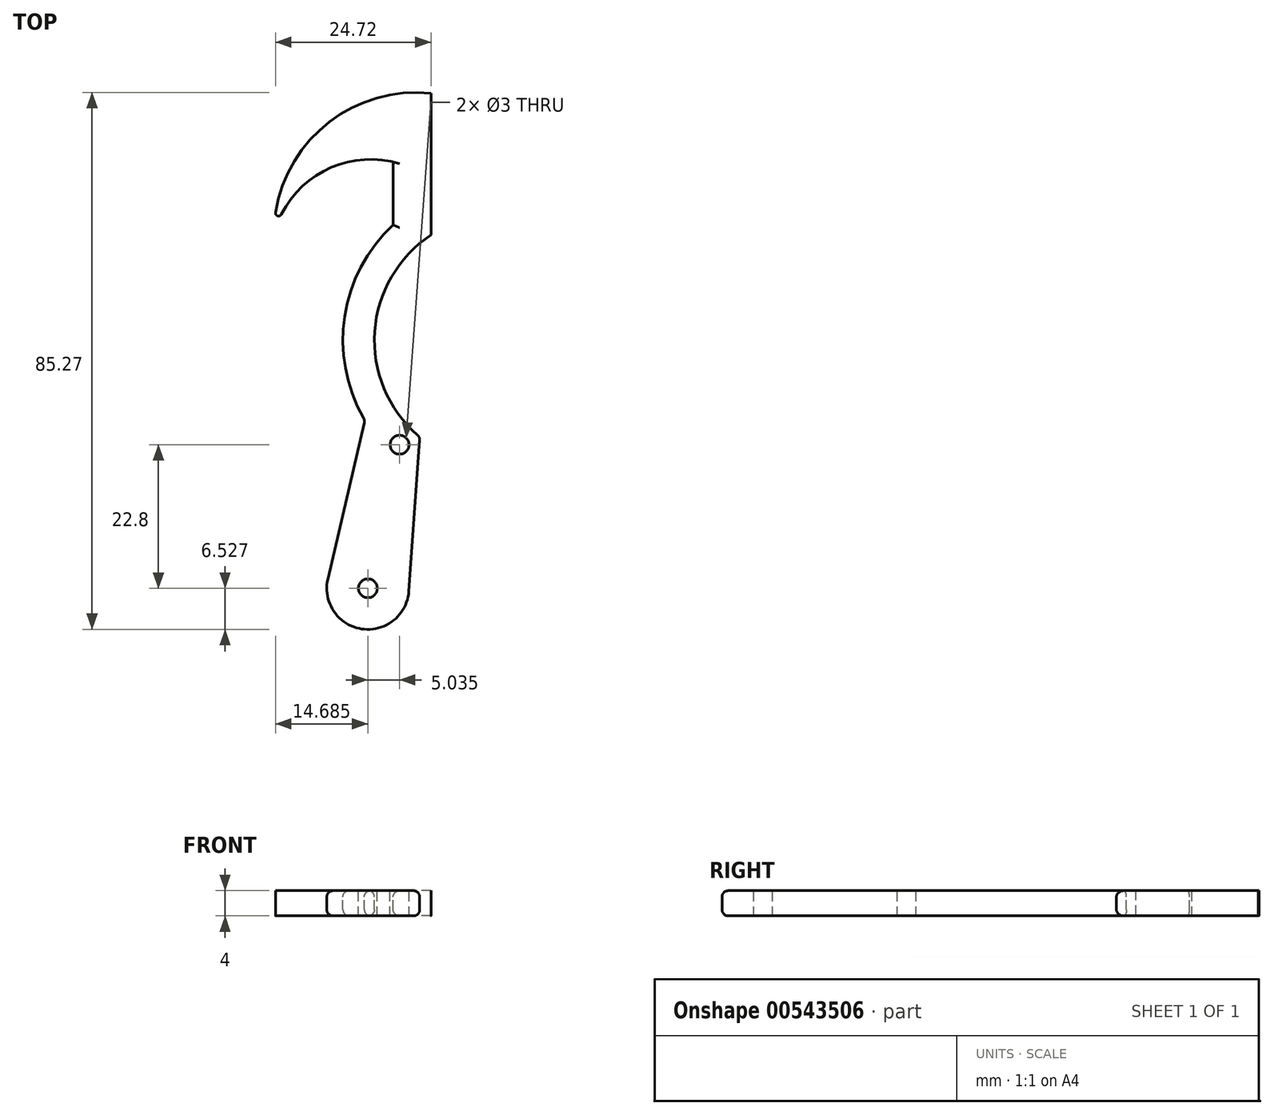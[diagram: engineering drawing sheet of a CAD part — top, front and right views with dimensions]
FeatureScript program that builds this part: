
annotation { "Feature Type Name" : "Feature", "Feature Type Description" : "" }
export const myFeature = defineFeature(function(context is Context, id is Id, definition is map)
    precondition{}
    {
        {
            var Q0;
            Q0=qCreatedBy(makeId("Top.planeOp"),FACE);
            var sketch = newSketch(context, id + "F0", { "sketchPlane" : qUnion([Q0])});
            skLineSegment(sketch, "E0", {"start": v(0, 17.48) * mm, "end": v(0, 40) * mm});
            skArc(sketch, "E1", {"start": v(0, 40) * mm, "mid": v(-17.51, 34.3) * mm, "end": v(-25, 17.48) * mm});
            skPoint(sketch, "E2.orphan", {"position": v(-25, 0) * mm});
            skArc(sketch, "E3", {"start": v(-6.01, 29.1) * mm, "mid": v(-17.88, 27.17) * mm, "end": v(-25, 17.48) * mm});
            skLineSegment(sketch, "E4", {"start": v(-6.01, 29.1) * mm, "end": v(-6.01, 19.1) * mm});
            skArc(sketch, "E5", {"start": v(0, 17.48) * mm, "mid": v(-8.95, 2.13) * mm, "end": v(-2.15, -14.28) * mm});
            skArc(sketch, "E6.0", {"start": v(-6.01, 19.1) * mm, "mid": v(-13.7, 4.58) * mm, "end": v(-10.72, -11.58) * mm});
            skPoint(sketch, "E7.orphan", {"position": v(-6.01, -34.64) * mm});
            skPoint(sketch, "E8.orphan", {"position": v(0, -34.64) * mm});
            skPoint(sketch, "E9.start.orphan", {"position": v(-6.01, 0) * mm});
            skPoint(sketch, "E10.visualSharp", {"position": v(4.84, -59.33) * mm});
            skLineSegment(sketch, "E11", {"start": v(-10.62, -12.3) * mm, "end": v(-16.4, -37.14) * mm});
            skPoint(sketch, "E12.orphan", {"position": v(0, -15.92) * mm});
            skPoint(sketch, "E13.visualSharp", {"position": v(-24.92, -73.81) * mm});
            skLineSegment(sketch, "E14.MirrorCS", {"start": v(-1.81, -15.1) * mm, "end": v(-3.52, -39.09) * mm});
            skPoint(sketch, "E15.orphan", {"position": v(-1.57, -11.78) * mm});
            skArc(sketch, "E16", {"start": v(-16.4, -37.14) * mm, "mid": v(-11, -45.08) * mm, "end": v(-3.52, -39.09) * mm});
            skPoint(sketch, "E17.visualSharp", {"position": v(-10.53, -11.92) * mm});
            skArc(sketch, "E17.filletArc", {"start": v(-10.62, -12.3) * mm, "mid": v(-10.6, -11.93) * mm, "end": v(-10.72, -11.58) * mm});
            skPoint(sketch, "E18.visualSharp", {"position": v(-1.77, -14.6) * mm});
            skArc(sketch, "E18.filletArc", {"start": v(-1.81, -15.1) * mm, "mid": v(-1.88, -14.65) * mm, "end": v(-2.15, -14.28) * mm});
            skSolve(sketch);
        }
        {
            var Q0;
            Q0=makeQuery(id+"F0.imprint","IMPRINT",FACE,{"disambiguationData":[TD([[makeQuery(id+"F0.imprint","IMPRINT",EDGE,{"derivedFrom":sQuery(id+"F0.wireOp",EDGE,"E0")}),1.0]])]});
            extrude(context, id + "F1", {"entities" : qUnion([Q0]), "oppositeDirection" : true, "depth" : 4 * mm, "offsetDistance" : 25.4 * mm});
        }
        {
            var Q0;
            Q0=makeQuery(id+"F1.opExtrude","SWEPT_EDGE",EDGE,{"disambiguationData":[OSD([sQuery(id+"F0.wireOp",EDGE,"E1"),sQuery(id+"F0.wireOp",EDGE,"E3")])]});
            fillet(context, id + "F2", {"entities" : qUnion([Q0]), "radius" : 0.5 * mm, "tangentPropagation" : true, "allowEdgeOverflow" : false});
        }
        {
            var Q0;
            Q0=makeQuery(id+"F1.opExtrude","CAP_EDGE",EDGE,{"disambiguationData":[OSD([sQuery(id+"F0.wireOp",EDGE,"E4")])],"isStart":true});
            var Q1;
            Q1=makeQuery(id+"F1.opExtrude","CAP_EDGE",EDGE,{"disambiguationData":[OSD([sQuery(id+"F0.wireOp",EDGE,"E4")])],"isStart":false});
            var Q2;
            Q2=makeQuery(id+"F1.opExtrude","CAP_EDGE",EDGE,{"disambiguationData":[OSD([sQuery(id+"F0.wireOp",EDGE,"E6.0")])],"isStart":true});
            var Q3;
            Q3=makeQuery(id+"F1.opExtrude","CAP_EDGE",EDGE,{"disambiguationData":[OSD([sQuery(id+"F0.wireOp",EDGE,"1G8ty3XP-Spk9-8nT8-YVZX-rUC8iMOiFmfu")])],"isStart":true});
            var Q4;
            Q4=makeQuery(id+"F1.opExtrude","CAP_EDGE",EDGE,{"disambiguationData":[OSD([sQuery(id+"F0.wireOp",EDGE,"E10.filletArc")])],"isStart":false});
            fillet(context, id + "F3", {"entities" : qUnion([Q0, Q1, Q2, Q3, Q4]), "radius" : 1 * mm, "tangentPropagation" : true, "allowEdgeOverflow" : false});
        }
        {
            var Q0;
            Q0=makeQuery(id+"F1.opExtrude","CAP_EDGE",EDGE,{"disambiguationData":[OSD([sQuery(id+"F0.wireOp",EDGE,"E6.0")])],"isStart":false});
            fillet(context, id + "F4", {"entities" : qUnion([Q0]), "radius" : 1 * mm, "tangentPropagation" : true, "allowEdgeOverflow" : false});
        }
        {
            var Q0;
            Q0=makeQuery(id+"F1.opExtrude","CAP_FACE",FACE,{"disambiguationData":[OSD([sQuery(id+"F0.wireOp",EDGE,"E0"),sQuery(id+"F0.wireOp",EDGE,"E1"),sQuery(id+"F0.wireOp",EDGE,"E3"),sQuery(id+"F0.wireOp",EDGE,"E4"),sQuery(id+"F0.wireOp",EDGE,"E5"),sQuery(id+"F0.wireOp",EDGE,"E6.0"),sQuery(id+"F0.wireOp",EDGE,"1G8ty3XP-Spk9-8nT8-YVZX-rUC8iMOiFmfu"),sQuery(id+"F0.wireOp",EDGE,"caZwswFN-XQGW-QiDH-Q43x-0XHMUoS2bRwR"),sQuery(id+"F0.wireOp",EDGE,"MjZZ4HA1-istc-ETjp-bfEB-5d9fU8IIfRrl"),sQuery(id+"F0.wireOp",EDGE,"29d1b39c-c66b-4002-b213-4030244decff.filletArc"),sQuery(id+"F0.wireOp",EDGE,"E10.filletArc")])],"isStart":true});
            var sketch = newSketch(context, id + "F5", { "sketchPlane" : qUnion([Q0])});
            skCircle(sketch, "E19", {"center": v(-5, -15.82) * mm, "radius": 1.5 * mm});
            skCircle(sketch, "E20", {"center": v(-10.03, -38.62) * mm, "radius": 1.5 * mm});
            skSolve(sketch);
        }
        {
            var Q0;
            Q0=makeQuery(id+"F5.imprint","IMPRINT",FACE,{"disambiguationData":[TD([[makeQuery(id+"F5.imprint","IMPRINT",EDGE,{"derivedFrom":sQuery(id+"F5.wireOp",EDGE,"E19")}),1.0]])]});
            var Q1;
            Q1=makeQuery(id+"F5.imprint","IMPRINT",FACE,{"disambiguationData":[TD([[makeQuery(id+"F5.imprint","IMPRINT",EDGE,{"derivedFrom":sQuery(id+"F5.wireOp",EDGE,"E20")}),1.0]])]});
            extrude(context, id + "F6", {"entities" : qUnion([Q0, Q1]), "operationType" : NewBodyOperationType.REMOVE, "oppositeDirection" : true, "depth" : 25.4 * mm, "offsetDistance" : 25.4 * mm});
        }
    });
